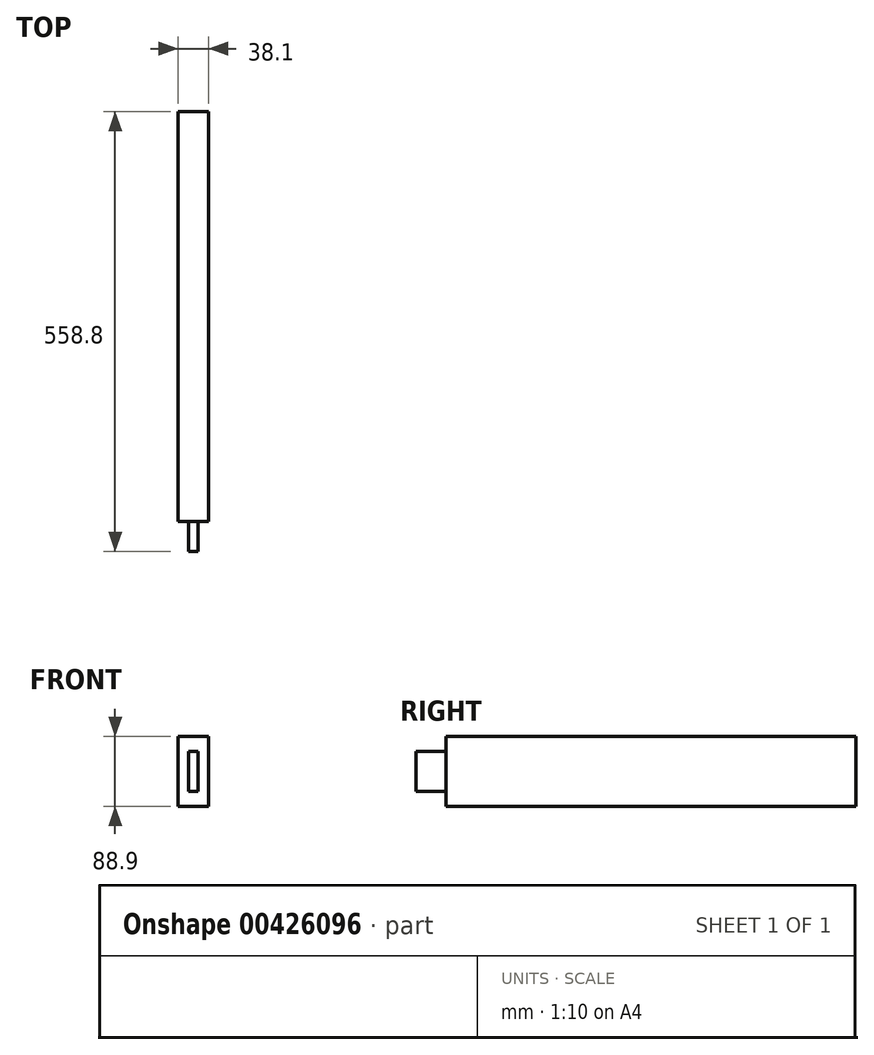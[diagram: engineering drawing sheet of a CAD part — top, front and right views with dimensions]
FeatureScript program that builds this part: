
annotation { "Feature Type Name" : "Feature", "Feature Type Description" : "" }
export const myFeature = defineFeature(function(context is Context, id is Id, definition is map)
    precondition{}
    {
        {
            var Q0;
            Q0=qCreatedBy(makeId("Front.planeOp"),FACE);
            var sketch = newSketch(context, id + "F0", { "sketchPlane" : qUnion([Q0])});
            skLineSegment(sketch, "E0.bottom", {"start": v(19.05, -44.45) * mm, "end": v(-19.05, -44.45) * mm});
            skLineSegment(sketch, "E0.top", {"start": v(19.05, 44.45) * mm, "end": v(-19.05, 44.45) * mm});
            skLineSegment(sketch, "E0.left", {"start": v(19.05, -44.45) * mm, "end": v(19.05, 44.45) * mm});
            skLineSegment(sketch, "E0.right", {"start": v(-19.05, -44.45) * mm, "end": v(-19.05, 44.45) * mm});
            skPoint(sketch, "E0.middle", {"position": v(0, 0) * mm});
            skSolve(sketch);
        }
        {
            var Q0;
            Q0=qSketchRegion(id+"F0",true);
            extrude(context, id + "F1", {"entities" : qUnion([Q0]), "endBound" : BoundingType.SYMMETRIC, "depth" : 558.8 * mm});
        }
        {
            var Q0;
            Q0=makeQuery(id+"F1.opExtrude","CAP_FACE",FACE,{"disambiguationData":[OSD([sQuery(id+"F0.wireOp",EDGE,"E0.bottom"),sQuery(id+"F0.wireOp",EDGE,"E0.top"),sQuery(id+"F0.wireOp",EDGE,"E0.left"),sQuery(id+"F0.wireOp",EDGE,"E0.right")])],"isStart":false});
            var sketch = newSketch(context, id + "F2", { "sketchPlane" : qUnion([Q0])});
            skLineSegment(sketch, "E1.bottom", {"start": v(-19.05, 44.45) * mm, "end": v(19.05, 44.45) * mm});
            skLineSegment(sketch, "E1.top", {"start": v(-19.05, -44.45) * mm, "end": v(19.05, -44.45) * mm});
            skLineSegment(sketch, "E1.left", {"start": v(-19.05, 44.45) * mm, "end": v(-19.05, -44.45) * mm});
            skLineSegment(sketch, "E1.right", {"start": v(19.05, 44.45) * mm, "end": v(19.05, -44.45) * mm});
            skLineSegment(sketch, "E2.bottom", {"start": v(6.35, -25.4) * mm, "end": v(-6.35, -25.4) * mm});
            skLineSegment(sketch, "E2.top", {"start": v(6.35, 25.4) * mm, "end": v(-6.35, 25.4) * mm});
            skLineSegment(sketch, "E2.left", {"start": v(6.35, -25.4) * mm, "end": v(6.35, 25.4) * mm});
            skLineSegment(sketch, "E2.right", {"start": v(-6.35, -25.4) * mm, "end": v(-6.35, 25.4) * mm});
            skPoint(sketch, "E2.middle", {"position": v(0, 0) * mm});
            skSolve(sketch);
        }
        {
            var Q0;
            Q0=qSketchRegion(id+"F2",true);
            extrude(context, id + "F3", {"entities" : qUnion([Q0]), "operationType" : NewBodyOperationType.REMOVE, "oppositeDirection" : true, "depth" : 38.1 * mm});
        }
    });
